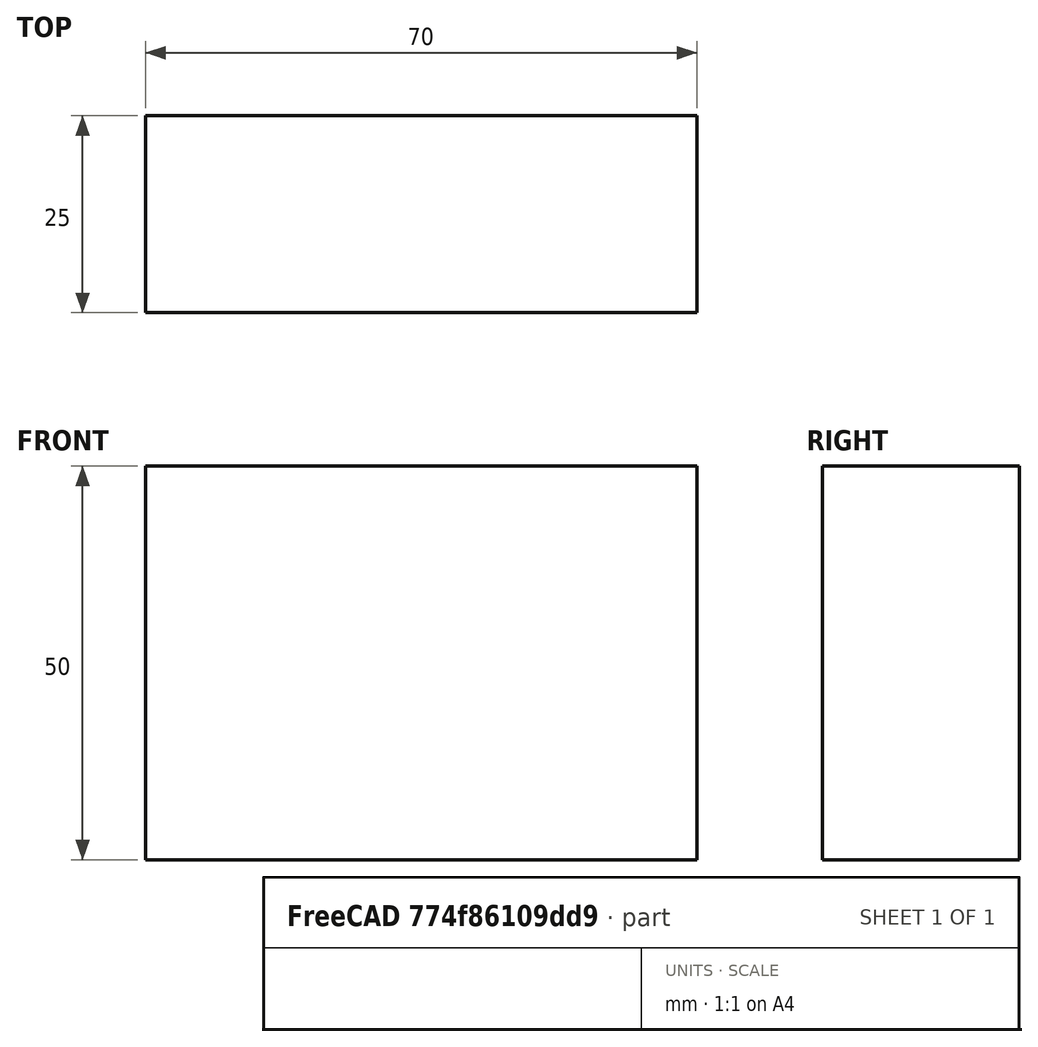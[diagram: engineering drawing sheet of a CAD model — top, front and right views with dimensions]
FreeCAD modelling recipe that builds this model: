
FCSTD DOCUMENT  (FreeCAD 0.15R4671 (Git))
Label: Flat Bar 70x25 EN10058 S235JR
License: All rights reserved
LicenseURL: http://en.wikipedia.org/wiki/All_rights_reserved
objects: Sketcher::SketchObject×1, Part::Extrusion×1
note: 2 computed .brp shape members not serialized (recipe doc carries the construction recipe); baked Part::Feature solids carry a one-line shape summary decoded from their .brp

FEATURE [Sketcher::SketchObject] Sketch
  sketch-geometry (4):
    g0: LineSegment StartX=-35 StartY=-12.5 StartZ=0 EndX=35 EndY=-12.5 EndZ=0
    g1: LineSegment StartX=35 StartY=-12.5 StartZ=0 EndX=35 EndY=12.5 EndZ=0
    g2: LineSegment StartX=35 StartY=12.5 StartZ=0 EndX=-35 EndY=12.5 EndZ=0
    g3: LineSegment StartX=-35 StartY=12.5 StartZ=0 EndX=-35 EndY=-12.5 EndZ=0
  constraints (12):
    c: Coincident(g0,g1)
    c: Coincident(g1,g2)
    c: Coincident(g2,g3)
    c: Coincident(g3,g0)
    c: Horizontal(g0)
    c: Horizontal(g2)
    c: Vertical(g1)
    c: Vertical(g3)
    c: Symmetric(g1,g2,g-2)
    c: Symmetric(g0,g1,g-1)
    c: DistanceY(g1) = 25
    c: DistanceX(g0) = 70
FEATURE [Part::Extrusion] Extrude  label="Flat Bar 70x25 EN10058 S235JR"
  Base = -> Sketch
  Dir = (0,0,50)
  Solid = true
